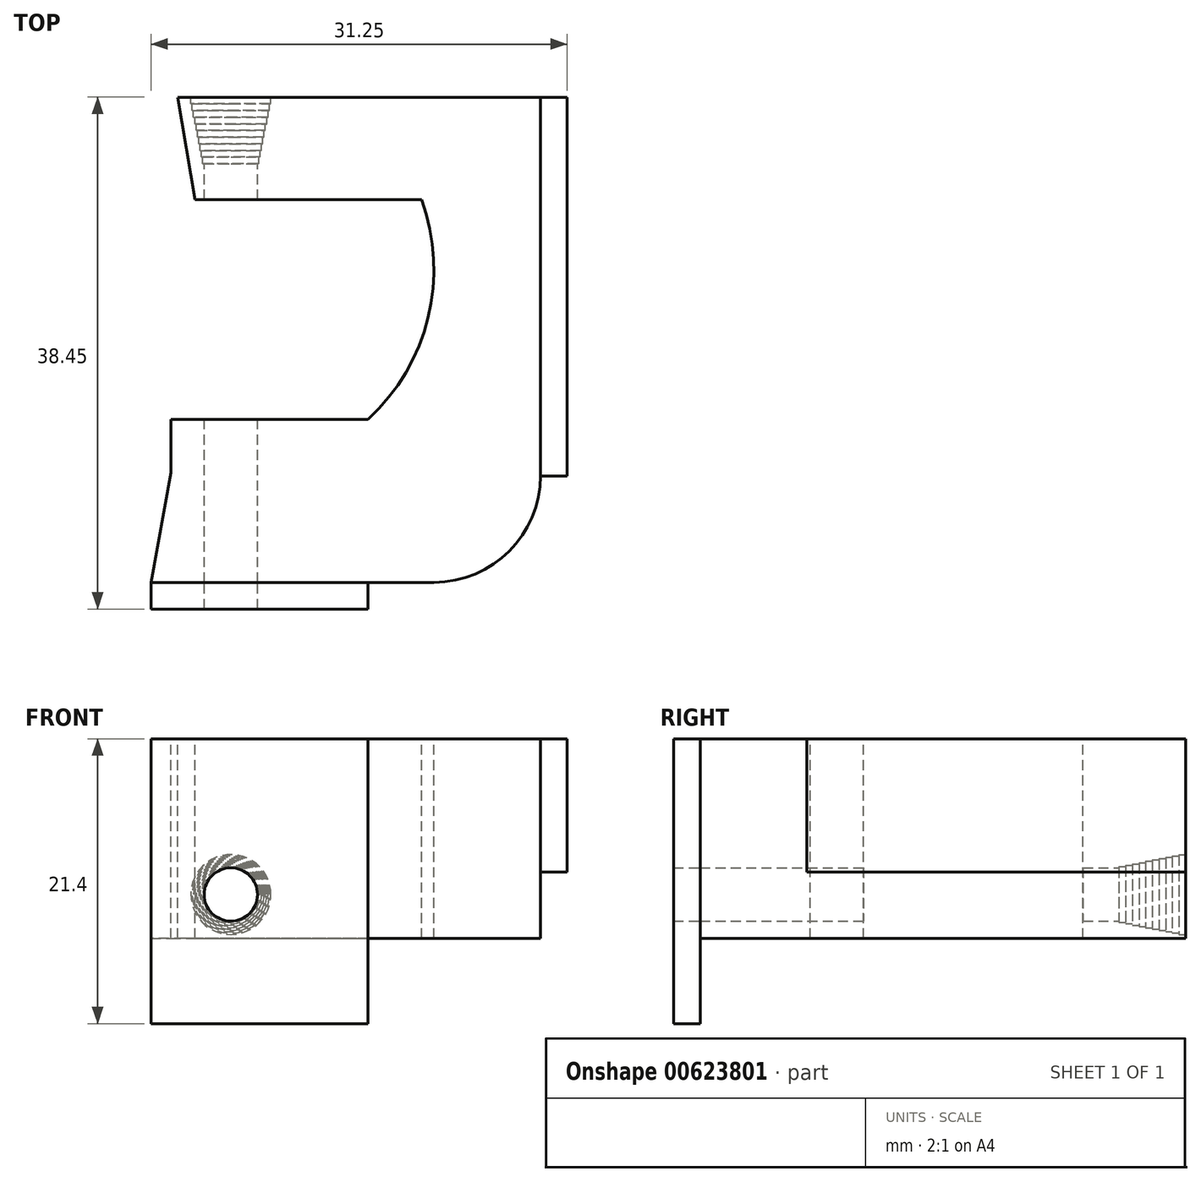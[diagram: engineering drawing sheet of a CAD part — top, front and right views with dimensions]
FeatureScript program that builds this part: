
annotation { "Feature Type Name" : "Feature", "Feature Type Description" : "" }
export const myFeature = defineFeature(function(context is Context, id is Id, definition is map)
    precondition{}
    {
        {
            var Q0;
            Q0=qCreatedBy(makeId("Top.planeOp"),FACE);
            var sketch = newSketch(context, id + "F0", { "sketchPlane" : qUnion([Q0])});
            skArc(sketch, "E0", {"start": v(0, -15.25) * mm, "mid": v(14.66, -4.2) * mm, "end": v(8.06, 12.95) * mm});
            skLineSegment(sketch, "E1", {"start": v(0, -23.5) * mm, "end": v(15.25, -23.5) * mm});
            skLineSegment(sketch, "E2", {"start": v(23.25, -15.5) * mm, "end": v(23.25, 21.52) * mm});
            skPoint(sketch, "E3.visualSharp", {"position": v(23.25, -23.5) * mm});
            skArc(sketch, "E3.filletArc", {"start": v(15.25, -23.5) * mm, "mid": v(20.9, -21.16) * mm, "end": v(23.25, -15.5) * mm});
            skLineSegment(sketch, "E4", {"start": v(0, -11.25) * mm, "end": v(10.3, -11.25) * mm});
            skLineSegment(sketch, "E5", {"start": v(0, -23.5) * mm, "end": v(-6, -23.5) * mm});
            skLineSegment(sketch, "E6", {"start": v(23.25, 12.95) * mm, "end": v(4, 12.95) * mm});
            skLineSegment(sketch, "E7", {"start": v(-2.7, 5.25) * mm, "end": v(-4, 12.95) * mm});
            skLineSegment(sketch, "E8", {"start": v(2.7, 5.25) * mm, "end": v(4, 12.95) * mm});
            skPoint(sketch, "E9.start.orphan", {"position": v(0, 15.25) * mm});
            skPoint(sketch, "E10.orphan", {"position": v(0, 12.95) * mm});
            skLineSegment(sketch, "E11", {"start": v(-4, 12.95) * mm, "end": v(4, 12.95) * mm});
            skLineSegment(sketch, "E12", {"start": v(-2.7, 5.25) * mm, "end": v(2.7, 5.25) * mm});
            skLineSegment(sketch, "E13", {"start": v(2.7, 5.25) * mm, "end": v(14.32, 5.25) * mm});
            skLineSegment(sketch, "E14", {"start": v(0, -15.25) * mm, "end": v(-4.5, -15.25) * mm});
            skLineSegment(sketch, "E15", {"start": v(-6, -23.5) * mm, "end": v(-4.5, -15.25) * mm});
            skLineSegment(sketch, "E16", {"start": v(-4.5, -15.25) * mm, "end": v(-4.5, -13.75) * mm});
            skLineSegment(sketch, "E17", {"start": v(-4.5, -13.75) * mm, "end": v(0, -11.25) * mm});
            skLineSegment(sketch, "E18", {"start": v(-6, -23.5) * mm, "end": v(-6, -25.5) * mm});
            skLineSegment(sketch, "E19", {"start": v(-6, -25.5) * mm, "end": v(10.3, -25.5) * mm});
            skLineSegment(sketch, "E20", {"start": v(10.3, -23.5) * mm, "end": v(10.3, -25.5) * mm});
            skLineSegment(sketch, "E21", {"start": v(23.25, -15.5) * mm, "end": v(25.25, -15.5) * mm});
            skLineSegment(sketch, "E22.bottom", {"start": v(23.25, 12.95) * mm, "end": v(25.25, 12.95) * mm});
            skLineSegment(sketch, "E22.left", {"start": v(23.25, 12.95) * mm, "end": v(23.25, -15.5) * mm});
            skLineSegment(sketch, "E22.right", {"start": v(25.25, 12.95) * mm, "end": v(25.25, -15.5) * mm});
            skLineSegment(sketch, "E23", {"start": v(0, -11.25) * mm, "end": v(-4.5, -11.25) * mm});
            skLineSegment(sketch, "E24", {"start": v(-4.5, -13.75) * mm, "end": v(-4.5, -11.25) * mm});
            skSolve(sketch);
        }
        {
            var Q0;
            Q0=makeQuery(id+"F0.imprint","IMPRINT",FACE,{"disambiguationData":[TD([[makeQuery(id+"F0.imprint","IMPRINT",EDGE,{"derivedFrom":sQuery(id+"F0.wireOp",EDGE,"E22.bottom")}),-1.0]])]});
            extrude(context, id + "F1", {"entities" : qUnion([Q0]), "oppositeDirection" : true, "depth" : 10 * mm, "offsetDistance" : 25 * mm});
        }
        {
            var Q0;
            {var subQ0=sQuery(id+"F0.wireOp",EDGE,"E5");Q0=makeQuery(id+"F0.imprint","IMPRINT",FACE,{"disambiguationData":[TD([[makeQuery(id+"F0.imprint","IMPRINT",EDGE,{"derivedFrom":subQ0}),1.0]])]});}
            extrude(context, id + "F2", {"entities" : qUnion([Q0]), "oppositeDirection" : true, "depth" : 21.4 * mm, "offsetDistance" : 25 * mm});
        }
        {
            var Q0;
            {var subQ5=sQuery(id+"F0.wireOp",EDGE,"E3.filletArc");Q0=makeQuery(id+"F0.imprint","IMPRINT",FACE,{"disambiguationData":[TD([[makeQuery(id+"F0.imprint","IMPRINT",EDGE,{"derivedFrom":subQ5}),1.0]])]});}
            var Q1;
            {var subQ0=sQuery(id+"F0.wireOp",EDGE,"E4");Q1=makeQuery(id+"F0.imprint","IMPRINT",FACE,{"disambiguationData":[TD([[makeQuery(id+"F0.imprint","IMPRINT",EDGE,{"derivedFrom":subQ0}),-1.0]])]});}
            var Q2;
            {var subQ4=sQuery(id+"F0.wireOp",EDGE,"E8");Q2=makeQuery(id+"F0.imprint","IMPRINT",FACE,{"disambiguationData":[TD([[makeQuery(id+"F0.imprint","IMPRINT",EDGE,{"derivedFrom":subQ4}),-1.0]])]});}
            var Q3;
            Q3=makeQuery(id+"F0.imprint","IMPRINT",FACE,{"disambiguationData":[TD([[makeQuery(id+"F0.imprint","IMPRINT",EDGE,{"derivedFrom":sQuery(id+"F0.wireOp",EDGE,"E7")}),-1.0]])]});
            var Q4;
            Q4=makeQuery(id+"F0.imprint","IMPRINT",FACE,{"disambiguationData":[TD([[makeQuery(id+"F0.imprint","IMPRINT",EDGE,{"derivedFrom":sQuery(id+"F0.wireOp",EDGE,"E17")}),1.0]])]});
            extrude(context, id + "F3", {"entities" : qUnion([Q0, Q1, Q2, Q3, Q4]), "oppositeDirection" : true, "depth" : 15 * mm, "offsetDistance" : 25 * mm});
        }
        {
            var Q0;
            Q0=makeQuery(id+"F3.opExtrude","SWEPT_FACE",FACE,{"disambiguationData":[OSD([sQuery(id+"F0.wireOp",EDGE,"E6"),sQuery(id+"F0.wireOp",EDGE,"E11")])]});
            var sketch = newSketch(context, id + "F4", { "sketchPlane" : qUnion([Q0])});
            skCircle(sketch, "E25", {"center": v(0, -11.7) * mm, "radius": 2 * mm});
            skCircle(sketch, "E26", {"center": v(0, -11.7) * mm, "radius": 2.1 * mm});
            skPoint(sketch, "E27.orphan", {"position": v(0, -15) * mm});
            skCircle(sketch, "E28", {"center": v(0, -11.7) * mm, "radius": 2.2 * mm});
            skCircle(sketch, "E29", {"center": v(0, -11.7) * mm, "radius": 2.3 * mm});
            skCircle(sketch, "E30", {"center": v(0, -11.7) * mm, "radius": 2.4 * mm});
            skCircle(sketch, "E31", {"center": v(0, -11.7) * mm, "radius": 2.5 * mm});
            skCircle(sketch, "E32", {"center": v(0, -11.7) * mm, "radius": 2.6 * mm});
            skCircle(sketch, "E33", {"center": v(0, -11.7) * mm, "radius": 2.7 * mm});
            skCircle(sketch, "E34", {"center": v(0, -11.7) * mm, "radius": 2.8 * mm});
            skCircle(sketch, "E35", {"center": v(0, -11.7) * mm, "radius": 2.9 * mm});
            skCircle(sketch, "E36", {"center": v(0, -11.7) * mm, "radius": 3 * mm});
            skSolve(sketch);
        }
        {
            var Q0;
            Q0=makeQuery(id+"F4.imprint","IMPRINT",FACE,{"disambiguationData":[TD([[makeQuery(id+"F4.imprint","IMPRINT",EDGE,{"derivedFrom":sQuery(id+"F4.wireOp",EDGE,"E25")}),1.0]])]});
            extrude(context, id + "F5", {"entities" : qUnion([Q0]), "operationType" : NewBodyOperationType.REMOVE, "oppositeDirection" : true, "depth" : 8 * mm, "offsetDistance" : 25 * mm});
        }
        {
            var Q0;
            Q0=makeQuery(id+"F4.imprint","IMPRINT",FACE,{"disambiguationData":[TD([[makeQuery(id+"F4.imprint","IMPRINT",EDGE,{"derivedFrom":sQuery(id+"F4.wireOp",EDGE,"E25")}),-1.0]])]});
            extrude(context, id + "F6", {"entities" : qUnion([Q0]), "operationType" : NewBodyOperationType.REMOVE, "oppositeDirection" : true, "depth" : 5 * mm, "offsetDistance" : 25 * mm});
        }
        {
            var Q0;
            Q0=makeQuery(id+"F4.imprint","IMPRINT",FACE,{"disambiguationData":[TD([[makeQuery(id+"F4.imprint","IMPRINT",EDGE,{"derivedFrom":sQuery(id+"F4.wireOp",EDGE,"E26")}),-1.0]])]});
            extrude(context, id + "F7", {"entities" : qUnion([Q0]), "operationType" : NewBodyOperationType.REMOVE, "oppositeDirection" : true, "depth" : 4.5 * mm, "offsetDistance" : 25 * mm});
        }
        {
            var Q0;
            Q0=makeQuery(id+"F4.imprint","IMPRINT",FACE,{"disambiguationData":[TD([[makeQuery(id+"F4.imprint","IMPRINT",EDGE,{"derivedFrom":sQuery(id+"F4.wireOp",EDGE,"E28")}),-1.0]])]});
            extrude(context, id + "F8", {"entities" : qUnion([Q0]), "operationType" : NewBodyOperationType.REMOVE, "oppositeDirection" : true, "depth" : 4 * mm, "offsetDistance" : 25 * mm});
        }
        {
            var Q0;
            Q0=makeQuery(id+"F4.imprint","IMPRINT",FACE,{"disambiguationData":[TD([[makeQuery(id+"F4.imprint","IMPRINT",EDGE,{"derivedFrom":sQuery(id+"F4.wireOp",EDGE,"E29")}),-1.0]])]});
            extrude(context, id + "F9", {"entities" : qUnion([Q0]), "operationType" : NewBodyOperationType.REMOVE, "oppositeDirection" : true, "depth" : 3.5 * mm, "offsetDistance" : 25 * mm});
        }
        {
            var Q0;
            Q0=makeQuery(id+"F4.imprint","IMPRINT",FACE,{"disambiguationData":[TD([[makeQuery(id+"F4.imprint","IMPRINT",EDGE,{"derivedFrom":sQuery(id+"F4.wireOp",EDGE,"E30")}),-1.0]])]});
            extrude(context, id + "F10", {"entities" : qUnion([Q0]), "operationType" : NewBodyOperationType.REMOVE, "oppositeDirection" : true, "depth" : 3 * mm, "offsetDistance" : 25 * mm});
        }
        {
            var Q0;
            Q0=makeQuery(id+"F4.imprint","IMPRINT",FACE,{"disambiguationData":[TD([[makeQuery(id+"F4.imprint","IMPRINT",EDGE,{"derivedFrom":sQuery(id+"F4.wireOp",EDGE,"E31")}),-1.0]])]});
            extrude(context, id + "F11", {"entities" : qUnion([Q0]), "operationType" : NewBodyOperationType.REMOVE, "oppositeDirection" : true, "depth" : 2.5 * mm, "offsetDistance" : 25 * mm});
        }
        {
            var Q0;
            Q0=makeQuery(id+"F4.imprint","IMPRINT",FACE,{"disambiguationData":[TD([[makeQuery(id+"F4.imprint","IMPRINT",EDGE,{"derivedFrom":sQuery(id+"F4.wireOp",EDGE,"E32")}),-1.0]])]});
            extrude(context, id + "F12", {"entities" : qUnion([Q0]), "operationType" : NewBodyOperationType.REMOVE, "oppositeDirection" : true, "depth" : 2 * mm, "offsetDistance" : 25 * mm});
        }
        {
            var Q0;
            Q0=makeQuery(id+"F4.imprint","IMPRINT",FACE,{"disambiguationData":[TD([[makeQuery(id+"F4.imprint","IMPRINT",EDGE,{"derivedFrom":sQuery(id+"F4.wireOp",EDGE,"E33")}),-1.0]])]});
            extrude(context, id + "F13", {"entities" : qUnion([Q0]), "operationType" : NewBodyOperationType.REMOVE, "oppositeDirection" : true, "depth" : 1.5 * mm, "offsetDistance" : 25 * mm});
        }
        {
            var Q0;
            Q0=makeQuery(id+"F4.imprint","IMPRINT",FACE,{"disambiguationData":[TD([[makeQuery(id+"F4.imprint","IMPRINT",EDGE,{"derivedFrom":sQuery(id+"F4.wireOp",EDGE,"E34")}),-1.0]])]});
            extrude(context, id + "F14", {"entities" : qUnion([Q0]), "operationType" : NewBodyOperationType.REMOVE, "oppositeDirection" : true, "depth" : 1 * mm, "offsetDistance" : 25 * mm});
        }
        {
            var Q0;
            Q0=makeQuery(id+"F4.imprint","IMPRINT",FACE,{"disambiguationData":[TD([[makeQuery(id+"F4.imprint","IMPRINT",EDGE,{"derivedFrom":sQuery(id+"F4.wireOp",EDGE,"E35")}),-1.0]])]});
            extrude(context, id + "F15", {"entities" : qUnion([Q0]), "operationType" : NewBodyOperationType.REMOVE, "oppositeDirection" : true, "depth" : .5 * mm, "offsetDistance" : 25 * mm});
        }
        {
            var Q0;
            Q0=makeQuery(id+"F3.opExtrude","SWEPT_FACE",FACE,{"disambiguationData":[OSD([sQuery(id+"F0.wireOp",EDGE,"E4"),sQuery(id+"F0.wireOp",EDGE,"E23")])]});
            var sketch = newSketch(context, id + "F16", { "sketchPlane" : qUnion([Q0])});
            skCircle(sketch, "E37", {"center": v(0, -11.7) * mm, "radius": 2 * mm});
            skPoint(sketch, "E38.start.orphan", {"position": v(0, -15) * mm});
            skCircle(sketch, "E39", {"center": v(0, -11.7) * mm, "radius": 2.1 * mm});
            skCircle(sketch, "E40", {"center": v(0, -11.7) * mm, "radius": 2.2 * mm});
            skCircle(sketch, "E41", {"center": v(0, -11.7) * mm, "radius": 2.3 * mm});
            skCircle(sketch, "E42", {"center": v(0, -11.7) * mm, "radius": 2.4 * mm});
            skCircle(sketch, "E43", {"center": v(0, -11.7) * mm, "radius": 2.5 * mm});
            skCircle(sketch, "E44", {"center": v(0, -11.7) * mm, "radius": 2.6 * mm});
            skCircle(sketch, "E45", {"center": v(0, -11.7) * mm, "radius": 2.7 * mm});
            skCircle(sketch, "E46", {"center": v(0, -11.7) * mm, "radius": 2.8 * mm});
            skCircle(sketch, "E47", {"center": v(0, -11.7) * mm, "radius": 2.9 * mm});
            skCircle(sketch, "E48", {"center": v(0, -11.7) * mm, "radius": 3 * mm});
            skSolve(sketch);
        }
        {
            var Q0;
            Q0=makeQuery(id+"F16.imprint","IMPRINT",FACE,{"disambiguationData":[TD([[makeQuery(id+"F16.imprint","IMPRINT",EDGE,{"derivedFrom":sQuery(id+"F16.wireOp",EDGE,"E37")}),1.0]])]});
            extrude(context, id + "F17", {"entities" : qUnion([Q0]), "operationType" : NewBodyOperationType.REMOVE, "oppositeDirection" : true, "depth" : 15 * mm, "offsetDistance" : 25 * mm});
        }
    });
